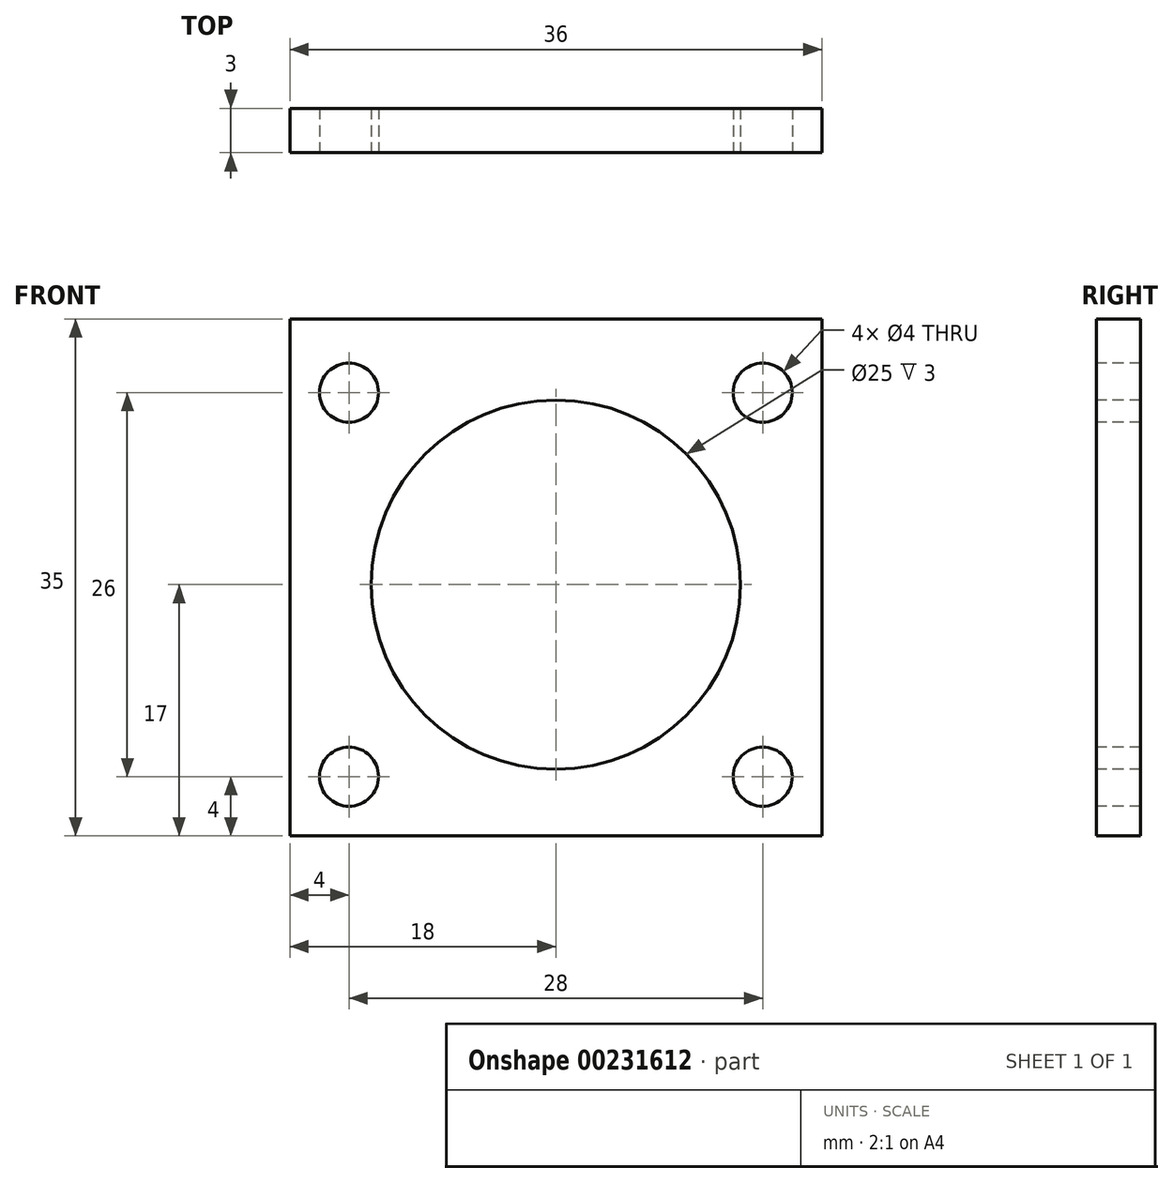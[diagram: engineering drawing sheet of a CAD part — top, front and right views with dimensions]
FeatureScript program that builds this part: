
annotation { "Feature Type Name" : "Feature", "Feature Type Description" : "" }
export const myFeature = defineFeature(function(context is Context, id is Id, definition is map)
    precondition{}
    {
        {
            var Q0;
            Q0=qCreatedBy(makeId("Front.planeOp"),FACE);
            var sketch = newSketch(context, id + "F0", { "sketchPlane" : qUnion([Q0])});
            skCircle(sketch, "E0", {"center": v(0, 0) * mm, "radius": 12.5 * mm});
            skCircle(sketch, "E1", {"center": v(0, 0) * mm, "radius": 15 * mm});
            skLineSegment(sketch, "E2.bottom", {"start": v(-18, 18) * mm, "end": v(18, 18) * mm});
            skLineSegment(sketch, "E2.top", {"start": v(-18, -17) * mm, "end": v(18, -17) * mm});
            skLineSegment(sketch, "E2.left", {"start": v(-18, 18) * mm, "end": v(-18, -17) * mm});
            skLineSegment(sketch, "E2.right", {"start": v(18, 18) * mm, "end": v(18, -17) * mm});
            skCircle(sketch, "E3", {"center": v(-14, 13) * mm, "radius": 2 * mm});
            skCircle(sketch, "E4", {"center": v(14, 13) * mm, "radius": 2 * mm});
            skCircle(sketch, "E5", {"center": v(14, -13) * mm, "radius": 2 * mm});
            skCircle(sketch, "E6", {"center": v(-14, -13) * mm, "radius": 2 * mm});
            skLineSegment(sketch, "E7", {"start": v(-14, 13) * mm, "end": v(14, 13) * mm, "construction": true});
            skLineSegment(sketch, "E8", {"start": v(14, -13) * mm, "end": v(14, 13) * mm, "construction": true});
            skLineSegment(sketch, "E9", {"start": v(14, -13) * mm, "end": v(-14, -13) * mm, "construction": true});
            skLineSegment(sketch, "E10", {"start": v(-14, -13) * mm, "end": v(-14, 13) * mm, "construction": true});
            skSolve(sketch);
        }
        {
            var Q0;
            Q0=makeQuery(id+"F0.imprint","IMPRINT",FACE,{"disambiguationData":[TD([[makeQuery(id+"F0.imprint","IMPRINT",EDGE,{"derivedFrom":sQuery(id+"F0.wireOp",EDGE,"E0")}),-1.0]])]});
            var Q1;
            Q1=makeQuery(id+"F0.imprint","IMPRINT",FACE,{"disambiguationData":[TD([[makeQuery(id+"F0.imprint","IMPRINT",EDGE,{"derivedFrom":sQuery(id+"F0.wireOp",EDGE,"E1")}),-1.0]])]});
            extrude(context, id + "F1", {"entities" : qUnion([Q0, Q1]), "oppositeDirection" : true, "depth" : 3 * mm});
        }
    });
